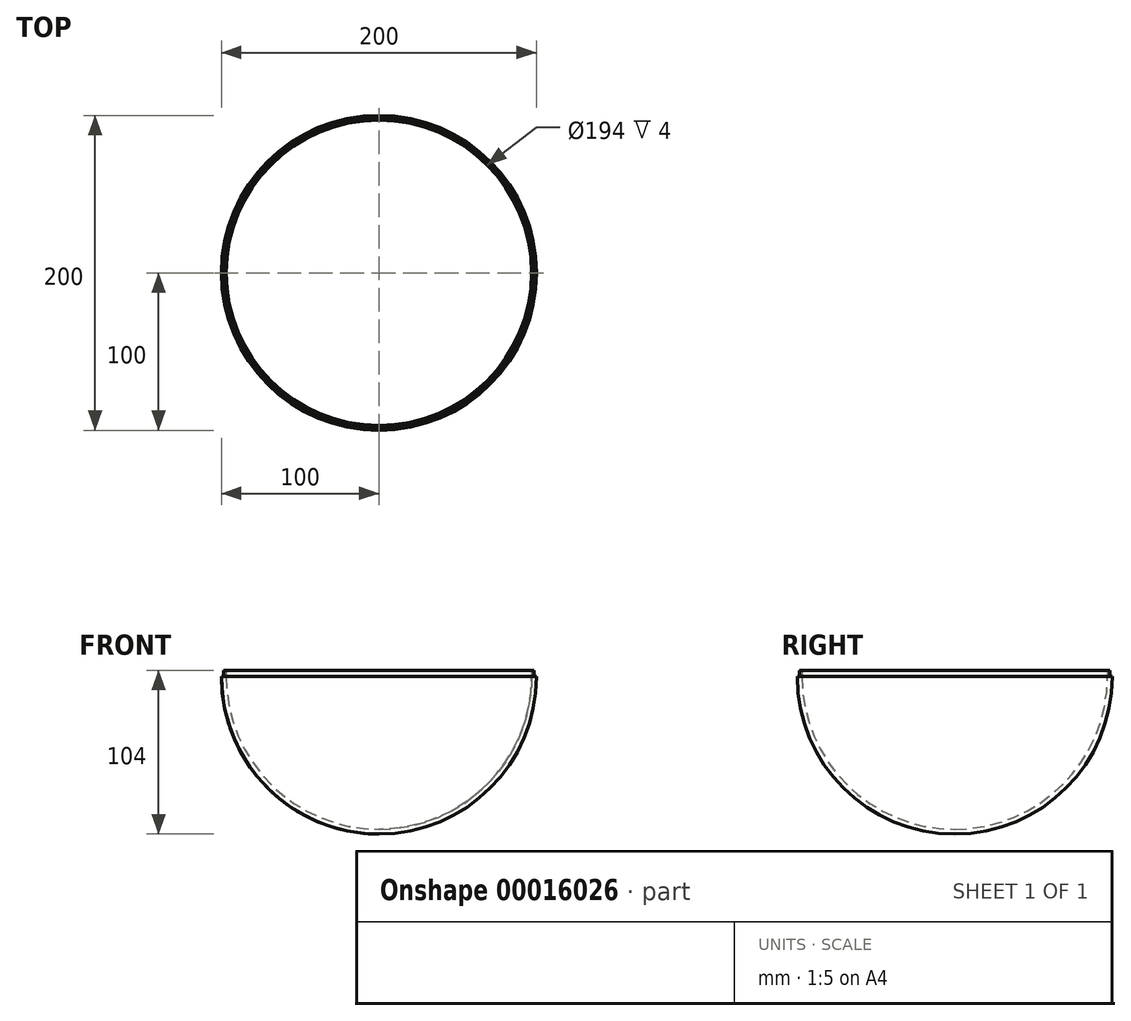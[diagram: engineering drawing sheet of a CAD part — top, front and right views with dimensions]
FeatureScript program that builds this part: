
annotation { "Feature Type Name" : "Feature", "Feature Type Description" : "" }
export const myFeature = defineFeature(function(context is Context, id is Id, definition is map)
    precondition{}
    {
        {
            var Q0;
            Q0=qCreatedBy(makeId("Front.planeOp"),FACE);
            var sketch = newSketch(context, id + "F0", { "sketchPlane" : qUnion([Q0])});
            skLineSegment(sketch, "E0", {"start": v(0, 0) * mm, "end": v(0, 100) * mm, "construction": true});
            skArc(sketch, "E1", {"start": v(0, -100) * mm, "mid": v(70.71, -70.71) * mm, "end": v(100, 0) * mm});
            skArc(sketch, "E2", {"start": v(0, -96.92) * mm, "mid": v(68.56, -68.54) * mm, "end": v(97, 0) * mm});
            skLineSegment(sketch, "E3", {"start": v(0, -96.92) * mm, "end": v(0, -100) * mm});
            skPoint(sketch, "E4.orphan", {"position": v(-97, 0) * mm});
            skPoint(sketch, "E5.orphan", {"position": v(-100, 0) * mm});
            skLineSegment(sketch, "E6", {"start": v(100, 0) * mm, "end": v(98.54, 0) * mm});
            skLineSegment(sketch, "E7", {"start": v(98.54, 0) * mm, "end": v(98.54, 4) * mm});
            skLineSegment(sketch, "E8", {"start": v(98.54, 4) * mm, "end": v(97, 4) * mm});
            skLineSegment(sketch, "E9", {"start": v(97, 4) * mm, "end": v(97, 0) * mm});
            skSolve(sketch);
        }
        {
            var Q0;
            Q0=makeQuery(id+"F0.imprint","IMPRINT",FACE,{"disambiguationData":[TD([[makeQuery(id+"F0.imprint","IMPRINT",EDGE,{"derivedFrom":sQuery(id+"F0.wireOp",EDGE,"E1")}),1.0]])]});
            var Q1;
            Q1=sQuery(id+"F0.wireOp",EDGE,"E0");
            revolve(context, id + "F1", {"entities" : qUnion([Q0]), "axis" : qUnion([Q1]), "revolveType" : RevolveType.FULL});
        }
    });
